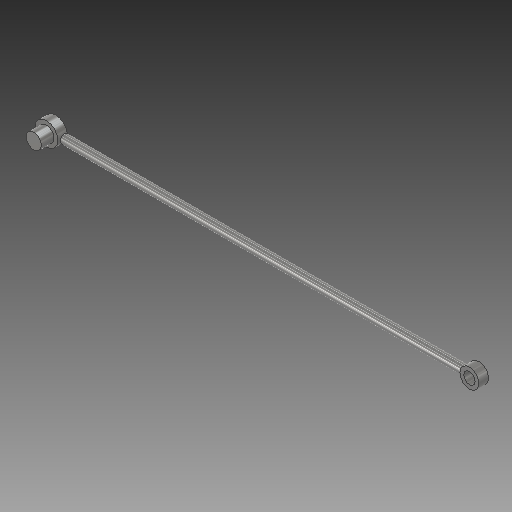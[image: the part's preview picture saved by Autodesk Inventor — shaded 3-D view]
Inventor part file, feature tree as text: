
AUTODESK INVENTOR PART (.ipt)
format: ipt  version: 2019 (Build 230136000, 136)  size: 136,192 bytes
history: native  units: mm
features: sketch x5, extrude x3, revolve x2, projected_geometry x1
ambient origin geometry x8: Origin, YZ Plane, XZ Plane, XY Plane, X Axis, Y Axis, Z Axis, Center Point
bodies: Solid1 (feature_tree)
feature tree (11):
  extrude  "Extrusion1"  Depth=105.0mm TaperAngle=0.0deg
  revolve  "Revolution1"  [1 undecoded]
  revolve  "Revolution2"  [1 undecoded]
  extrude  "Extrusion2"  Depth=0.5mm
  extrude  "Extrusion3"  TaperAngle=90.0deg  [1 undecoded]
  sketch  "Sketch1"  dims[d0=2.3mm d1=105.0mm d2=0.0mm]
  sketch  "Sketch3"  dims[d7=2.5mm d10=1.0mm]
  sketch  "Sketch4"  dims[d11=0.5mm d12=2.5mm]
  sketch  "Sketch5"  dims[d13=90.0deg d14=0.5mm]
  projected_geometry  "Projected Loop1"
  sketch  "Sketch6"  dims[d18=3.0mm d19=90.0deg d20=4.0mm d21=3.3mm d22=0.0mm d23=0.3mm d24=0.0mm]
note: 3 required parameter values undecoded (feature->parameter linkage not recoverable at this tier; creation-order binding heuristic only, values carry confidence <= 0.55)